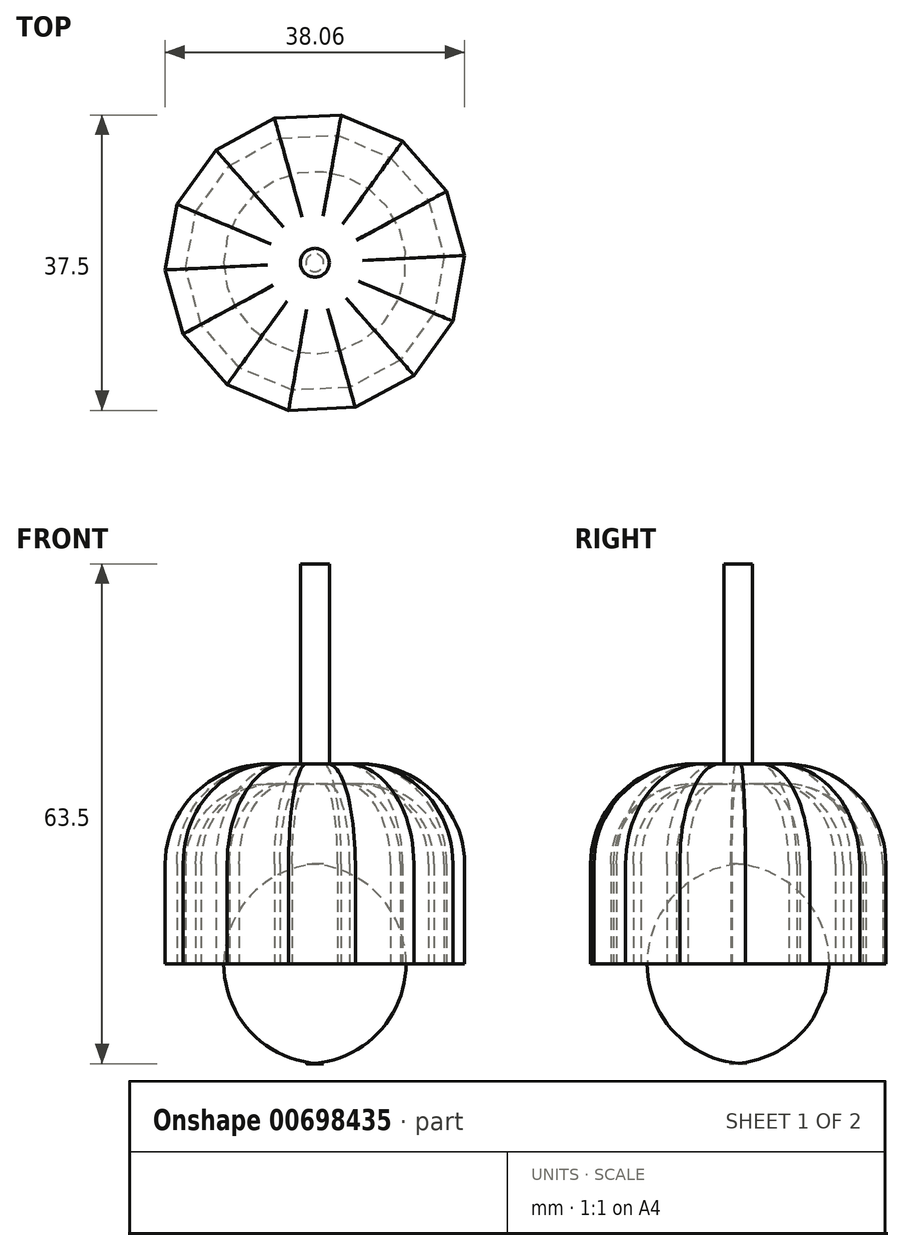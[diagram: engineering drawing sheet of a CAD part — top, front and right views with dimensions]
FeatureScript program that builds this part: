
annotation { "Feature Type Name" : "Feature", "Feature Type Description" : "" }
export const myFeature = defineFeature(function(context is Context, id is Id, definition is map)
    precondition{}
    {
        {
            var Q0;
            Q0=qCreatedBy(makeId("Top.planeOp"),FACE);
            var sketch = newSketch(context, id + "F0", { "sketchPlane" : qUnion([Q0])});
            skCircle(sketch, "E0.cCircle", {"center": v(0, 0) * mm, "radius": 18.57 * mm, "construction": true});
            skLineSegment(sketch, "E0.0", {"start": v(-12.58, 14.3) * mm, "end": v(-5.13, 18.35) * mm});
            skLineSegment(sketch, "E0.1", {"start": v(-5.13, 18.35) * mm, "end": v(3.34, 18.75) * mm});
            skLineSegment(sketch, "E0.2", {"start": v(3.34, 18.75) * mm, "end": v(11.15, 15.45) * mm});
            skLineSegment(sketch, "E0.3", {"start": v(11.15, 15.45) * mm, "end": v(16.75, 9.08) * mm});
            skLineSegment(sketch, "E0.4", {"start": v(16.75, 9.08) * mm, "end": v(19.03, 0.92) * mm});
            skLineSegment(sketch, "E0.5", {"start": v(19.03, 0.92) * mm, "end": v(17.54, -7.43) * mm});
            skLineSegment(sketch, "E0.6", {"start": v(17.54, -7.43) * mm, "end": v(12.58, -14.3) * mm});
            skLineSegment(sketch, "E0.7", {"start": v(12.58, -14.3) * mm, "end": v(5.13, -18.35) * mm});
            skLineSegment(sketch, "E0.8", {"start": v(5.13, -18.35) * mm, "end": v(-3.34, -18.75) * mm});
            skLineSegment(sketch, "E0.9", {"start": v(-3.34, -18.75) * mm, "end": v(-11.15, -15.45) * mm});
            skLineSegment(sketch, "E0.10", {"start": v(-11.15, -15.45) * mm, "end": v(-16.75, -9.08) * mm});
            skLineSegment(sketch, "E0.11", {"start": v(-16.75, -9.08) * mm, "end": v(-19.03, -0.92) * mm});
            skLineSegment(sketch, "E0.12", {"start": v(-19.03, -0.92) * mm, "end": v(-17.54, 7.43) * mm});
            skLineSegment(sketch, "E0.13", {"start": v(-17.54, 7.43) * mm, "end": v(-12.58, 14.3) * mm});
            skPoint(sketch, "E0.0.midPoint", {"position": v(-8.85, 16.33) * mm});
            skSolve(sketch);
        }
        {
            var Q0;
            Q0=makeQuery(id+"F0.imprint","IMPRINT",FACE,{"disambiguationData":[TD([[makeQuery(id+"F0.imprint","IMPRINT",EDGE,{"derivedFrom":sQuery(id+"F0.wireOp",EDGE,"E0.0")}),-1.0]])]});
            extrude(context, id + "F1", {"entities" : qUnion([Q0]), "depth" : 25.4 * mm, "offsetDistance" : 25.4 * mm});
        }
        {
            var Q0;
            Q0=makeQuery(id+"F1.opExtrude","CAP_EDGE",EDGE,{"disambiguationData":[OSD([sQuery(id+"F0.wireOp",EDGE,"E0.8")])],"isStart":false});
            var Q1;
            Q1=makeQuery(id+"F1.opExtrude","CAP_EDGE",EDGE,{"disambiguationData":[OSD([sQuery(id+"F0.wireOp",EDGE,"E0.6")])],"isStart":false});
            var Q2;
            Q2=makeQuery(id+"F1.opExtrude","CAP_EDGE",EDGE,{"disambiguationData":[OSD([sQuery(id+"F0.wireOp",EDGE,"E0.7")])],"isStart":false});
            var Q3;
            Q3=makeQuery(id+"F1.opExtrude","CAP_EDGE",EDGE,{"disambiguationData":[OSD([sQuery(id+"F0.wireOp",EDGE,"E0.5")])],"isStart":false});
            var Q4;
            Q4=makeQuery(id+"F1.opExtrude","CAP_EDGE",EDGE,{"disambiguationData":[OSD([sQuery(id+"F0.wireOp",EDGE,"E0.4")])],"isStart":false});
            var Q5;
            Q5=makeQuery(id+"F1.opExtrude","CAP_EDGE",EDGE,{"disambiguationData":[OSD([sQuery(id+"F0.wireOp",EDGE,"E0.3")])],"isStart":false});
            var Q6;
            Q6=makeQuery(id+"F1.opExtrude","CAP_EDGE",EDGE,{"disambiguationData":[OSD([sQuery(id+"F0.wireOp",EDGE,"E0.2")])],"isStart":false});
            var Q7;
            Q7=makeQuery(id+"F1.opExtrude","CAP_EDGE",EDGE,{"disambiguationData":[OSD([sQuery(id+"F0.wireOp",EDGE,"E0.1")])],"isStart":false});
            var Q8;
            Q8=makeQuery(id+"F1.opExtrude","CAP_EDGE",EDGE,{"disambiguationData":[OSD([sQuery(id+"F0.wireOp",EDGE,"E0.0")])],"isStart":false});
            var Q9;
            Q9=makeQuery(id+"F1.opExtrude","CAP_EDGE",EDGE,{"disambiguationData":[OSD([sQuery(id+"F0.wireOp",EDGE,"E0.13")])],"isStart":false});
            var Q10;
            Q10=makeQuery(id+"F1.opExtrude","CAP_FACE",FACE,{"disambiguationData":[OSD([sQuery(id+"F0.wireOp",EDGE,"E0.0"),sQuery(id+"F0.wireOp",EDGE,"E0.1"),sQuery(id+"F0.wireOp",EDGE,"E0.2"),sQuery(id+"F0.wireOp",EDGE,"E0.3"),sQuery(id+"F0.wireOp",EDGE,"E0.4"),sQuery(id+"F0.wireOp",EDGE,"E0.5"),sQuery(id+"F0.wireOp",EDGE,"E0.6"),sQuery(id+"F0.wireOp",EDGE,"E0.7"),sQuery(id+"F0.wireOp",EDGE,"E0.8"),sQuery(id+"F0.wireOp",EDGE,"E0.9"),sQuery(id+"F0.wireOp",EDGE,"E0.10"),sQuery(id+"F0.wireOp",EDGE,"E0.11"),sQuery(id+"F0.wireOp",EDGE,"E0.12"),sQuery(id+"F0.wireOp",EDGE,"E0.13")])],"isStart":false});
            fillet(context, id + "F2", {"entities" : qUnion([Q0, Q1, Q2, Q3, Q4, Q5, Q6, Q7, Q8, Q9, Q10]), "radius" : 12.7 * mm, "tangentPropagation" : true, "allowEdgeOverflow" : false});
        }
        {
            var Q0;
            Q0=makeQuery(id+"F1.opExtrude","CAP_FACE",FACE,{"disambiguationData":[OSD([sQuery(id+"F0.wireOp",EDGE,"E0.0"),sQuery(id+"F0.wireOp",EDGE,"E0.1"),sQuery(id+"F0.wireOp",EDGE,"E0.2"),sQuery(id+"F0.wireOp",EDGE,"E0.3"),sQuery(id+"F0.wireOp",EDGE,"E0.4"),sQuery(id+"F0.wireOp",EDGE,"E0.5"),sQuery(id+"F0.wireOp",EDGE,"E0.6"),sQuery(id+"F0.wireOp",EDGE,"E0.7"),sQuery(id+"F0.wireOp",EDGE,"E0.8"),sQuery(id+"F0.wireOp",EDGE,"E0.9"),sQuery(id+"F0.wireOp",EDGE,"E0.10"),sQuery(id+"F0.wireOp",EDGE,"E0.11"),sQuery(id+"F0.wireOp",EDGE,"E0.12"),sQuery(id+"F0.wireOp",EDGE,"E0.13")])],"isStart":false});
            var sketch = newSketch(context, id + "F3", { "sketchPlane" : qUnion([Q0])});
            skCircle(sketch, "E1", {"center": v(0, 0) * mm, "radius": 1.83 * mm});
            skSolve(sketch);
        }
        {
            var Q0;
            Q0=makeQuery(id+"F3.imprint","IMPRINT",FACE,{"disambiguationData":[TD([[makeQuery(id+"F3.imprint","IMPRINT",EDGE,{"derivedFrom":sQuery(id+"F3.wireOp",EDGE,"E1")}),1.0]])]});
            extrude(context, id + "F4", {"entities" : qUnion([Q0]), "operationType" : NewBodyOperationType.ADD, "depth" : 25.4 * mm, "offsetDistance" : 25.4 * mm});
        }
        {
            var Q0;
            Q0=makeQuery(id+"F1.opExtrude","CAP_FACE",FACE,{"disambiguationData":[OSD([sQuery(id+"F0.wireOp",EDGE,"E0.0"),sQuery(id+"F0.wireOp",EDGE,"E0.1"),sQuery(id+"F0.wireOp",EDGE,"E0.2"),sQuery(id+"F0.wireOp",EDGE,"E0.3"),sQuery(id+"F0.wireOp",EDGE,"E0.4"),sQuery(id+"F0.wireOp",EDGE,"E0.5"),sQuery(id+"F0.wireOp",EDGE,"E0.6"),sQuery(id+"F0.wireOp",EDGE,"E0.7"),sQuery(id+"F0.wireOp",EDGE,"E0.8"),sQuery(id+"F0.wireOp",EDGE,"E0.9"),sQuery(id+"F0.wireOp",EDGE,"E0.10"),sQuery(id+"F0.wireOp",EDGE,"E0.11"),sQuery(id+"F0.wireOp",EDGE,"E0.12"),sQuery(id+"F0.wireOp",EDGE,"E0.13")])],"isStart":true});
            shell(context, id + "F5", {"entities" : qUnion([Q0]), "thickness" : 2.54 * mm});
        }
        {
            var Q0;
            Q0=qCreatedBy(makeId("Top.planeOp"),FACE);
            var sketch = newSketch(context, id + "F6", { "sketchPlane" : qUnion([Q0])});
            skCircle(sketch, "E2", {"center": v(0, 0) * mm, "radius": 13.82 * mm});
            skSolve(sketch);
        }
        {
            var Q0;
            Q0=makeQuery(id+"F6.imprint","IMPRINT",FACE,{"disambiguationData":[TD([[makeQuery(id+"F6.imprint","IMPRINT",EDGE,{"derivedFrom":sQuery(id+"F6.wireOp",EDGE,"E2")}),1.0]])]});
            extrude(context, id + "F7", {"entities" : qUnion([Q0]), "oppositeDirection" : true, "depth" : 12.7 * mm, "offsetDistance" : 25.4 * mm});
        }
        {
            var Q0;
            Q0=makeQuery(id+"F7.opExtrude","CAP_EDGE",EDGE,{"disambiguationData":[OSD([sQuery(id+"F6.wireOp",EDGE,"E2")])],"isStart":false});
            fillet(context, id + "F8", {"entities" : qUnion([Q0]), "radius" : 12.7 * mm, "tangentPropagation" : true, "allowEdgeOverflow" : false});
        }
        {
            var Q0;
            Q0=makeQuery(id+"F7.opExtrude","SWEPT_BODY",BODY,{"disambiguationData":[OSD([sQuery(id+"F6.wireOp",EDGE,"E2")])]});
            var Q1;
            Q1=qCreatedBy(makeId("Top.planeOp"),FACE);
            mirror(context, id + "F9", {"operationType" : NewBodyOperationType.ADD, "entities" : qUnion([Q0]), "mirrorPlane" : qUnion([Q1])});
        }
    });
